# Revit family: 145_HL310NPrG
name_source: partatom
category: Instalační zařizovací předměty
revit_build: Autodesk Revit 2016 (Build: 20150714_1515(x64)
units: mm (PartAtom-declared; Revit-internal decimal feet)

## family parameters
Bod výpočtu místnosti = Ano
Kóta kulaté spojky = Použít průměr
Nadpis OmniClass = Deck Waste Water Drains
Ořezat dutým tvarem při načtení = Ne
Sdílené = Ano
Typ součásti = Normální
Vždy vertikální = Ano
Založené na pracovní rovině = Ne
Číslo OmniClass = 23.70.50.21.24.14

## types (1)
- HL310NPrG
    EAN = 9003076004690
    Klíčová poznámka = HL310NPrG
    Komentáře k typům = HL310NPrG Трап для внутренних помещений DN50/75/110 вертикальный с запахозапирающим устройством Primus, 150х150мм/137х137мм чугун.
    Model = HL310NPrG
    Popis = Трапы для внутренних помещений
    Připojení CW = Ne
    Připojení HW = Ne
    Připojení odpadu = Ano
    Připojení ventilace = Ne
    URL = http://www.hutterer-lechner.com
    Výrobce = HL Hutterer & Lechner GmbH
    ВЕС = 2,43 [kg]
    ВЫСОТА МОНТАЖА = 179 mm
    МАКСИМАЛЬНАЯ НАГРУЗКА КЛАССА = A/L15 - 1,5 t
    МАТЕРИАЛ = PE
    НАСАДКА = 35-75 mm / 150 x 150 mm / GJL
    НОМИНАЛЬНЫЙ ДИАМЕТР = 110 mm
    ПРОИЗВОДИТЕЛЬНОСТЬ = 0,5 l/s
    ПРОПУСКНАЯ СПОСОБНОСТЬ = 0.5 L/s
    РАЗМЕР = DN50/75/110
    РЕШЁТКА = 137 x 137 mm / GJL

## geometry (parser evidence)
native form markers: Sweep x39
no freeform markers — native parametric forms only
